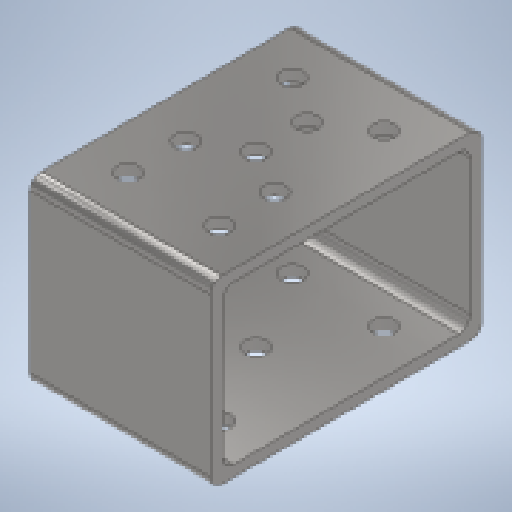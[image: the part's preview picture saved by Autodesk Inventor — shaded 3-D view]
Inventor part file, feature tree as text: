
AUTODESK INVENTOR PART (.ipt)
format: ipt  version: 2025.2 (Build 292293000, 293)  size: 192,512 bytes
history: native  units: in
note: dims shown in document units (in); Inventor stores cm internally (conversion verified against a paired STEP export)
features: extrude x5, sketch x2, shell x1, fillet x1
ambient origin geometry x8: Origin, YZ Plane, XZ Plane, XY Plane, X Axis, Y Axis, Z Axis, Center Point
bodies: Solid1 (feature_tree)
feature tree (9):
  extrude  "Extrusion1"  Depth=2.0in
  shell  "Shell1"  Thickness=2.0in
  fillet  "Fillet1"  Radius=0.125in
  extrude  "Extrusion2"  Depth=2.0in
  extrude  "Extrusion4"  Depth=2.0in
  extrude  "Extrusion3"  Depth=3.0in
  extrude  "Extrusion5"  Depth=2.0in
  sketch  "Sketch4"  dims[d0=3.0in d1=2.0in d2=2.0in d3=0.0in d4=0.125in]
  sketch  "Sketch5"  dims[d5=0.125in d6=0.25in d7=2.0in d8=3.0in d10=0.4921in d11=0.5906in d12=0.0in d13=0.0in d14=0.125in d15=3.0in d16=2.0in d17=0.25in d21=1.0in d22=0.0in d23=0.25in d24=1.0in d25=0.0in d26=0.0in d27=0.0in d28=0.9843in]
